# Revit family: 1240_P-HLOS-KP_nailfin_HP
name_source: partatom
category: Doors
revit_build: Autodesk Revit 2016 (Build: 20190507_1515(x64)
units: mm (PartAtom-declared; Revit-internal decimal feet)

## family parameters
Always vertical = Yes
Cut with Voids When Loaded = No
Host = Wall
OmniClass Number = 23.30.20.00
OmniClass Title = Windows
Room Calculation Point = No
Shared = No

## types (43) — shared parameters
Closed = No
Default Sill Height = 0"
Open = Yes
Setback = 1 1/8"
Wall Closure = By host

## per-type parameters (varying)
| type | Bar set | HBS | Height | Sash Width | Width_x |
| 96X96 | 39 1/4" | 12" | 96" | 36 1/4" | 96" |
| 35X92min | 23" | 12" | 92" | 20" | 35" |
| 35X96 | 23" | 12" | 96" | 20" | 35" |
| 96X92 | 39 1/4" | 12" | 92" | 36 1/4" | 96" |
| 42X92 | 30" | 12" | 92" | 27" | 42" |
| 42X96 | 30" | 12" | 96" | 27" | 42" |
| 48X92 | 36" | 12" | 92" | 33" | 48" |
| 48X96 | 36" | 12" | 96" | 33" | 48" |
| 90X92 | 39 1/4" | 12" | 92" | 36 1/4" | 90" |
| 90X96 | 39 1/4" | 12" | 96" | 36 1/4" | 90" |
| 84X92 | 39 1/4" | 12" | 92" | 36 1/4" | 84" |
| 84X96 | 39 1/4" | 12" | 96" | 36 1/4" | 84" |
| 78X92 | 39 1/4" | 12" | 92" | 36 1/4" | 78" |
| 78X96 | 39 1/4" | 12" | 96" | 36 1/4" | 78" |
| 66X92 | 39 1/4" | 12" | 92" | 36 1/4" | 66" |
| 66X96 | 39 1/4" | 12" | 96" | 36 1/4" | 66" |
| 60X92 | 39 1/4" | 12" | 92" | 36 1/4" | 60" |
| 60X96 | 39 1/4" | 12" | 96" | 36 1/4" | 60" |
| 54X92 | 39 1/4" | 12" | 92" | 36 1/4" | 54" |
| 54X96 | 39 1/4" | 12" | 96" | 36 1/4" | 54" |
| 72X92 | 39 1/4" | 12" | 92" | 36 1/4" | 72" |
| 72X96 | 39 1/4" | 12" | 96" | 36 1/4" | 72" |
| 96X120max | 39 1/4" | 24" | 120" | 36 1/4" | 96" |
| 42X102 | 30" | 18" | 102" | 27" | 42" |
| 48X102 | 36" | 18" | 102" | 33" | 48" |
| 54X102 | 39 1/4" | 18" | 102" | 36 1/4" | 54" |
| 60X102 | 39 1/4" | 18" | 102" | 36 1/4" | 60" |
| 60X108 | 39 1/4" | 18" | 108" | 36 1/4" | 60" |
| 66X102 | 39 1/4" | 18" | 102" | 36 1/4" | 66" |
| 66X108 | 39 1/4" | 18" | 108" | 36 1/4" | 66" |
| 72X102 | 39 1/4" | 18" | 102" | 36 1/4" | 72" |
| 72X108 | 39 1/4" | 18" | 108" | 36 1/4" | 72" |
| 78X102 | 39 1/4" | 18" | 102" | 36 1/4" | 78" |
| 78X108 | 39 1/4" | 18" | 108" | 36 1/4" | 78" |
| 84X102 | 39 1/4" | 18" | 102" | 36 1/4" | 84" |
| 84X108 | 39 1/4" | 18" | 108" | 36 1/4" | 84" |
| 90X102 | 39 1/4" | 18" | 102" | 36 1/4" | 90" |
| 90X108 | 39 1/4" | 18" | 108" | 36 1/4" | 90" |
| 96X102 | 39 1/4" | 18" | 102" | 36 1/4" | 96" |
| 96X108 | 39 1/4" | 18" | 108" | 36 1/4" | 96" |
| 96X114 | 39 1/4" | 18" | 114" | 36 1/4" | 96" |
| 90X114 | 39 1/4" | 18" | 114" | 36 1/4" | 90" |
| 90X120 | 39 1/4" | 24" | 120" | 36 1/4" | 90" |

## geometry (parser evidence)
native form markers: Sweep x3
no freeform markers — native parametric forms only
